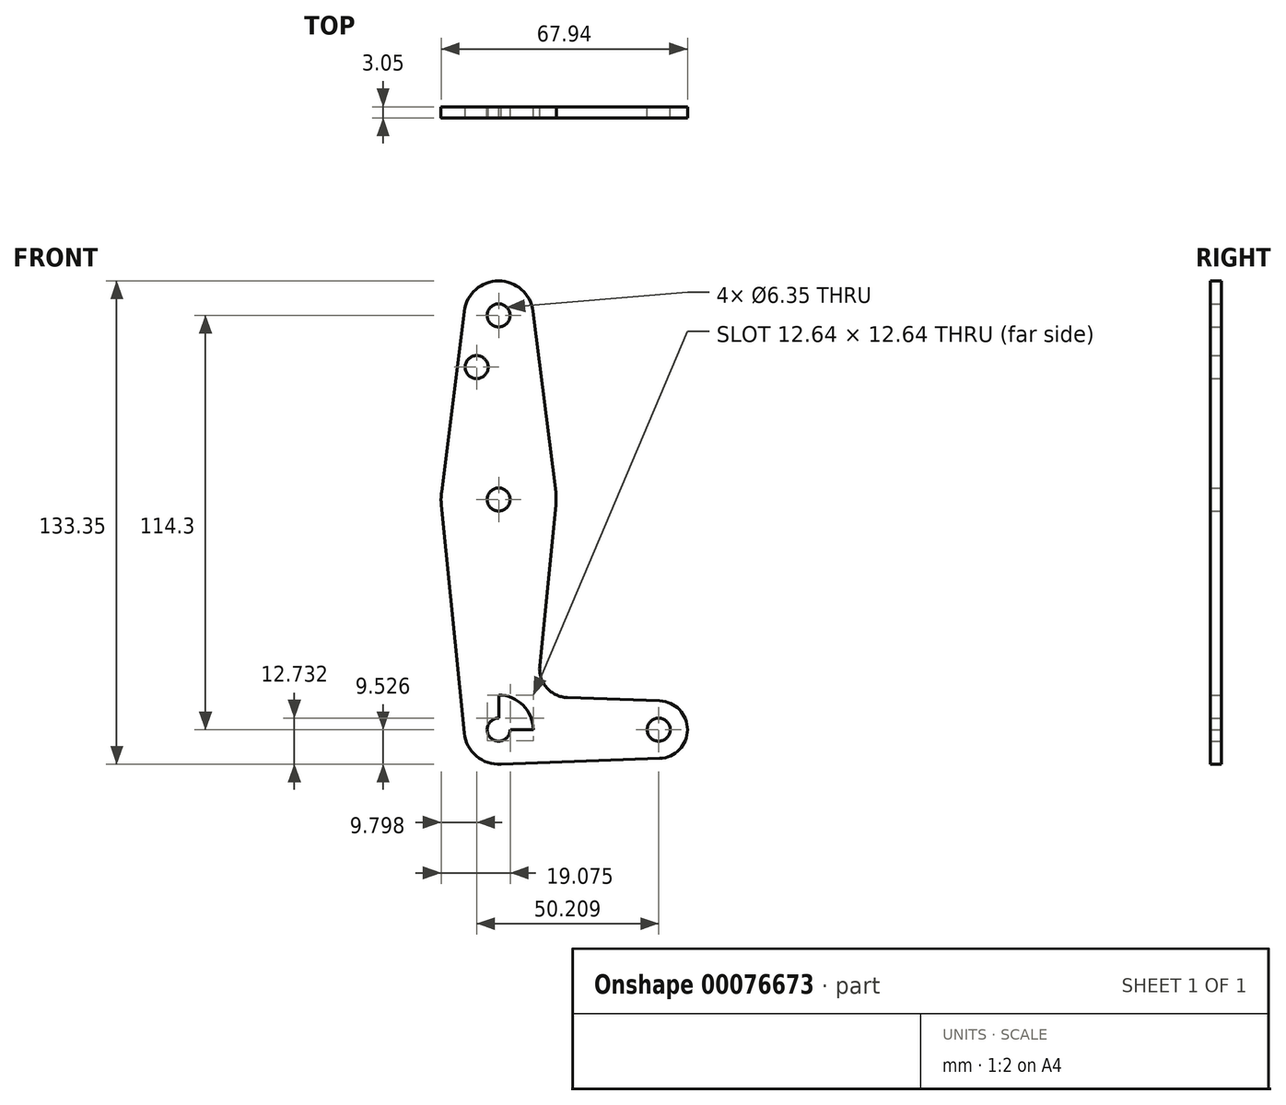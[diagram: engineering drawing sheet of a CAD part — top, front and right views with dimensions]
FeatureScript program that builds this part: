
annotation { "Feature Type Name" : "Feature", "Feature Type Description" : "" }
export const myFeature = defineFeature(function(context is Context, id is Id, definition is map)
    precondition{}
    {
        {
            var Q0;
            Q0=qCreatedBy(makeId("Front.planeOp"),FACE);
            var sketch = newSketch(context, id + "F0", { "sketchPlane" : qUnion([Q0])});
            skLineSegment(sketch, "E0", {"start": v(0, 57.2) * mm, "end": v(0, -57.1) * mm});
            skCircle(sketch, "E1", {"center": v(0, 6.4) * mm, "radius": 15.88 * mm});
            skCircle(sketch, "E2", {"center": v(0, -57.1) * mm, "radius": 9.53 * mm});
            skLineSegment(sketch, "E3", {"start": v(0, 6.4) * mm, "end": v(0, -57.1) * mm});
            skLineSegment(sketch, "E4", {"start": v(0, -57.1) * mm, "end": v(44.14, -57.1) * mm});
            skCircle(sketch, "E5", {"center": v(44.14, -57.1) * mm, "radius": 7.94 * mm});
            skLineSegment(sketch, "E6", {"start": v(-15.8, 4.82) * mm, "end": v(-9.48, -58.05) * mm});
            skLineSegment(sketch, "E7", {"start": v(15.8, 4.82) * mm, "end": v(11.34, -39.5) * mm});
            skCircle(sketch, "E8", {"center": v(0, 57.2) * mm, "radius": 9.53 * mm});
            skLineSegment(sketch, "E9", {"start": v(-9.45, 58.4) * mm, "end": v(-15.75, 8.4) * mm});
            skCircle(sketch, "E10", {"center": v(0, 57.2) * mm, "radius": 3.18 * mm});
            skLineSegment(sketch, "E11", {"start": v(9.45, 58.4) * mm, "end": v(15.75, 8.4) * mm});
            skLineSegment(sketch, "E12", {"start": v(18.97, -48.25) * mm, "end": v(44.42, -49.16) * mm});
            skLineSegment(sketch, "E13", {"start": v(0, -66.62) * mm, "end": v(44.42, -65.03) * mm});
            skCircle(sketch, "E14", {"center": v(0, 6.4) * mm, "radius": 3.18 * mm});
            skCircle(sketch, "E15", {"center": v(0, -57.1) * mm, "radius": 3.18 * mm});
            skCircle(sketch, "E16", {"center": v(44.14, -57.1) * mm, "radius": 3.18 * mm});
            skPoint(sketch, "E17.newPointA", {"position": v(9.48, -58.05) * mm});
            skPoint(sketch, "E17.newPointB", {"position": v(0, -47.57) * mm});
            skArc(sketch, "E17.filletArc", {"start": v(11.34, -39.5) * mm, "mid": v(13.26, -45.53) * mm, "end": v(18.97, -48.25) * mm});
            skLineSegment(sketch, "E18", {"start": v(0, 6.4) * mm, "end": v(0, 42.93) * mm});
            skCircle(sketch, "E19", {"center": v(-6.07, 42.93) * mm, "radius": 3.18 * mm});
            skSolve(sketch);
        }
        {
            var Q0;
            Q0 = qSketchRegion(id + "F0", true);
            var Q1;
            {var subQ0=sQuery(id+"F0.wireOp",EDGE,"E3");var subQ1=sQuery(id+"F0.wireOp",EDGE,"E2");var subQ2=makeQuery(id+"F0.imprint","INTERSECT",VERTEX,{"derivedFrom":[subQ1,subQ0]});Q1=makeQuery(id+"F0.imprint","IMPRINT",FACE,{"disambiguationData":[TD([[makeQuery(id+"F0.imprint","IMPRINT",EDGE,{"disambiguationData":[TD([[subQ2,1.0]])],"derivedFrom":subQ1}),1.0]])]});}
            extrude(context, id + "F1", {"entities" : qUnion([Q0, Q1]), "depth" : 3.05 * mm});
        }
    });
